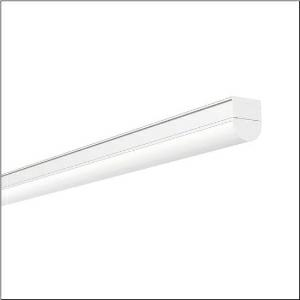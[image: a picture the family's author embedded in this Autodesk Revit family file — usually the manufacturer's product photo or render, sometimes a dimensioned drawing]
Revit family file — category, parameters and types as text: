
# Revit family: ecopack_r__31_51lj12mdm20a_29c1
name_source: partatom
category: Lighting Fixtures
units: mm (PartAtom-declared; Revit-internal decimal feet)

## family parameters
Cut with Voids When Loaded = No
Host = Face
Light Source = No
Part Type = Normal
Room Calculation Point = No
Round Connector Dimension = Use Diameter
Shared = No

## types (1)
- --- (1 x LED, 2510 lm, 20 W, 5000K)
    Apparent Load = 20 VA
    CIE Flux Codes = 41 71 90 93 100
    Color Rendering = 80
    Color Temperature = 5000K
    Default Elevation = 1800 mm
    Description = Ecopack® 31, diffuser luminaire, primary optical cover: cover, of PC, frosted, light emission: direct distribution, primary light characteristic: symmetric, installation type: surface-mounted, LED, rated luminous flux: 2.600lm, luminous efficacy: 130lm/W, light colour: 830/840/850, colour temperature: 3000/4000/5000K, control gear: ON/OFF Multilumen, with terminal, 3-pole, mains connection: 220..240V, AC, 50/60Hz, rated input power: 20W, housing, of aluminium, traffic white (RAL 9016), length: 600mm, width: 56mm, height: 68mm, end cap, of PC, white, protection rating (complete): IP20, insulation class (complete): insulation class I (protective earthing), certification: CE, impact resistance: IK06, permissible operating ambient temperature: -20..+40°C, packaging unit: 1 piece
    Height = 68 mm
    Lamp = 1 x LED
    Lamp Light Flux = 2510 lm
    Lamp Power = 20 W
    Lamp count = 1
    Length = 600 mm
    Luminous efficacy = 126 lm/W
    Manufacturer = Siteco
    ModVariant = No
    Model = 51LJ12MDM20A
    Mounting Place = Ceiling
    Mounting Type = Surface mounted
    Number of Poles = 1
    OnlyDefault = Yes
    Power Factor = 1
    Product Name = Ecopack® 31
    Product group = diffuser luminaire
    ProductGroupID = 307
    Protection Class = Protection class I
    Protection Degree = IP 20
    RLX_Detail_Level = 1
    RLX_Emergency_Light_Flux = 0 lm
    RLX_Emergency_Type = 0
    RLX_Emergency_Type_DB = No
    RlxData = <blob elided: 25481 chars, md5=d12eb985>
    Socket = socket
    Standby Power = 0 W
    System Light Flux = 2510 lm
    System Power = 20 W
    Type Comments = individual setting: colour temperature 5000K, luminous flux: 100 % | (ON | ON)
    Type Image = l_1007030.jpg
    URL = http://relux.com
    VarID = @adj_195529
    Voltage = 0 V
    Weight = 0.00 kg
    Width = 56 mm

## geometry (parser evidence)
native form markers: Blend x4, Sweep x12
no freeform markers — native parametric forms only
